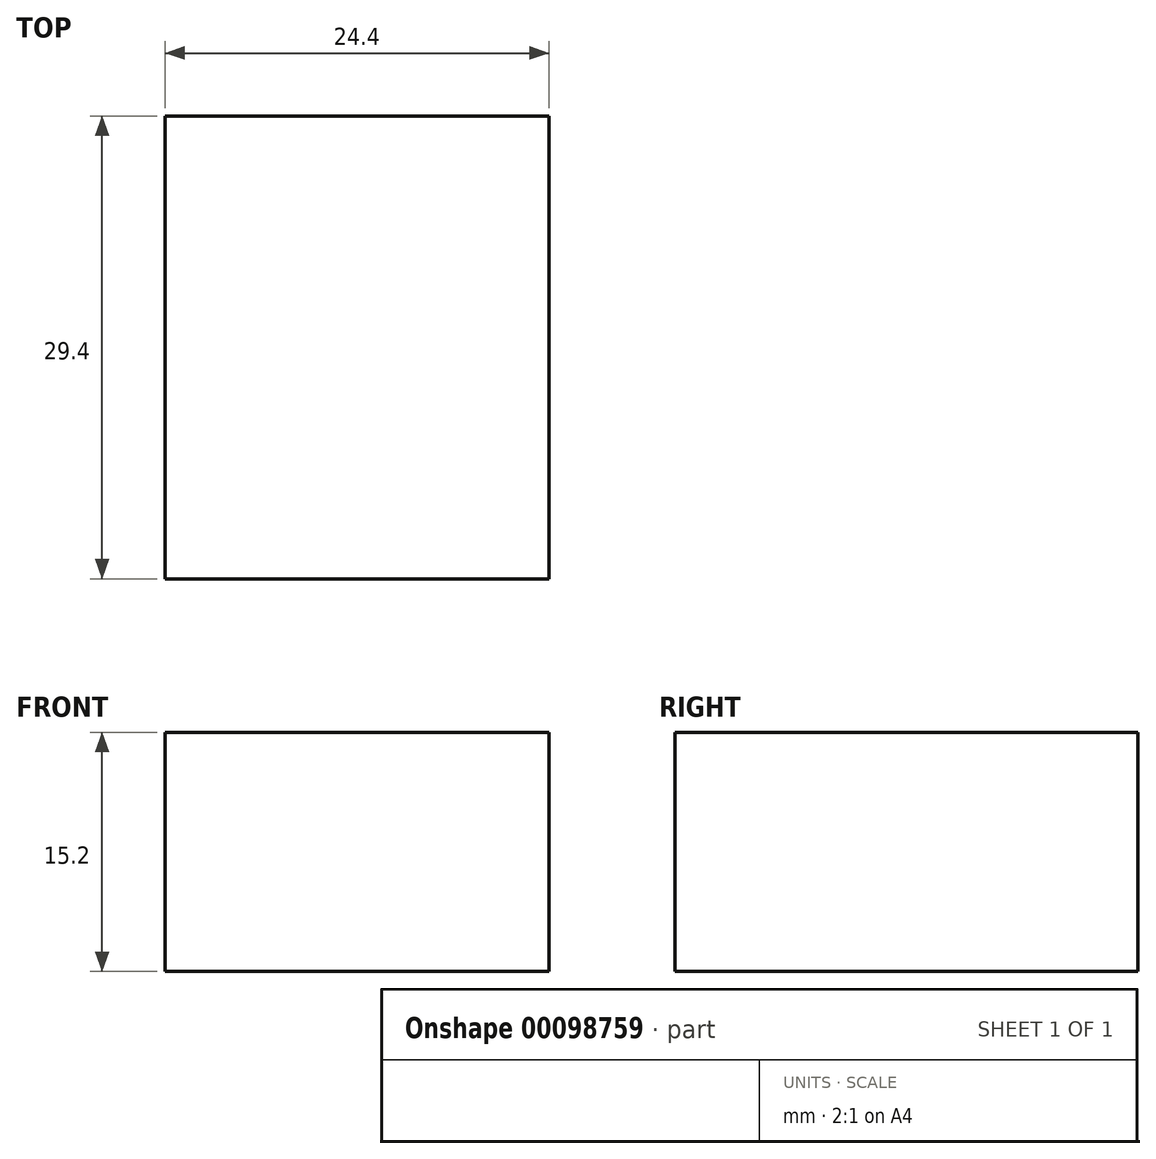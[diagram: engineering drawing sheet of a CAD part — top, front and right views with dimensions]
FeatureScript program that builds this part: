
annotation { "Feature Type Name" : "Feature", "Feature Type Description" : "" }
export const myFeature = defineFeature(function(context is Context, id is Id, definition is map)
    precondition{}
    {
        {
            var Q0;
            Q0=qCreatedBy(makeId("Front.planeOp"),FACE);
            var sketch = newSketch(context, id + "F0", { "sketchPlane" : qUnion([Q0])});
            skLineSegment(sketch, "E0", {"start": v(-12.2, 7.6) * mm, "end": v(-12.2, -7.6) * mm});
            skLineSegment(sketch, "E1", {"start": v(-12.2, -7.6) * mm, "end": v(12.2, -7.6) * mm});
            skLineSegment(sketch, "E2", {"start": v(12.2, -7.6) * mm, "end": v(12.2, 7.6) * mm});
            skLineSegment(sketch, "E3", {"start": v(12.2, 7.6) * mm, "end": v(-12.2, 7.6) * mm});
            skSolve(sketch);
        }
        {
            var Q0;
            Q0 = qSketchRegion(id + "F0", true);
            extrude(context, id + "F1", {"entities" : qUnion([Q0]), "oppositeDirection" : true, "depth" : 29.4 * mm});
        }
    });
